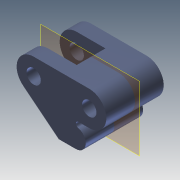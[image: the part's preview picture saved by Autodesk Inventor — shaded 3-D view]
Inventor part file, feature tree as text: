
AUTODESK INVENTOR PART (.ipt)
format: ipt  version: 2011 (Build 150229000, 229)  size: 134,144 bytes
history: native  units: mm (DEFAULTED — no unit token found)
features: extrude x2, hole x2, sketch x2
ambient origin geometry x8: Origin, YZ Plane, XZ Plane, XY Plane, X Axis, Y Axis, Z Axis, Center Point
bodies: Solid1 (feature_tree)
feature tree (6):
  extrude  "Extrusion1"  Depth=8.0mm
  extrude  "Extrusion2"  Depth=1.5mm
  hole  "Hole1"  [1 undecoded]
  hole  "Hole2"  [1 undecoded]
  sketch  "Sketch1"  dims[d0=9.5mm d1=8.0mm]
  sketch  "Sketch2"  dims[d2=31.0mm d3=1.5mm d4=5.5mm d6=9.512966mm d7=6.743535mm d9=32.840229mm d10=16.910363mm d11=32.0mm d12=0.0mm d13=2.0mm d14=16.0mm d15=32.0mm d16=0.0mm d17=10.0mm d18=10.0mm d19=8.0mm d20=6.0mm d21=4.0mm d22=2.0mm d23=90.0deg d24=8.0mm d25=20.594885mm d26=10.0mm d27=10.0mm d28=8.0mm d29=6.0mm d30=4.0mm d31=2.0mm d32=90.0deg d33=8.0mm d34=20.594885mm]
note: 2 required parameter values undecoded (feature->parameter linkage not recoverable at this tier; creation-order binding heuristic only, values carry confidence <= 0.55)
